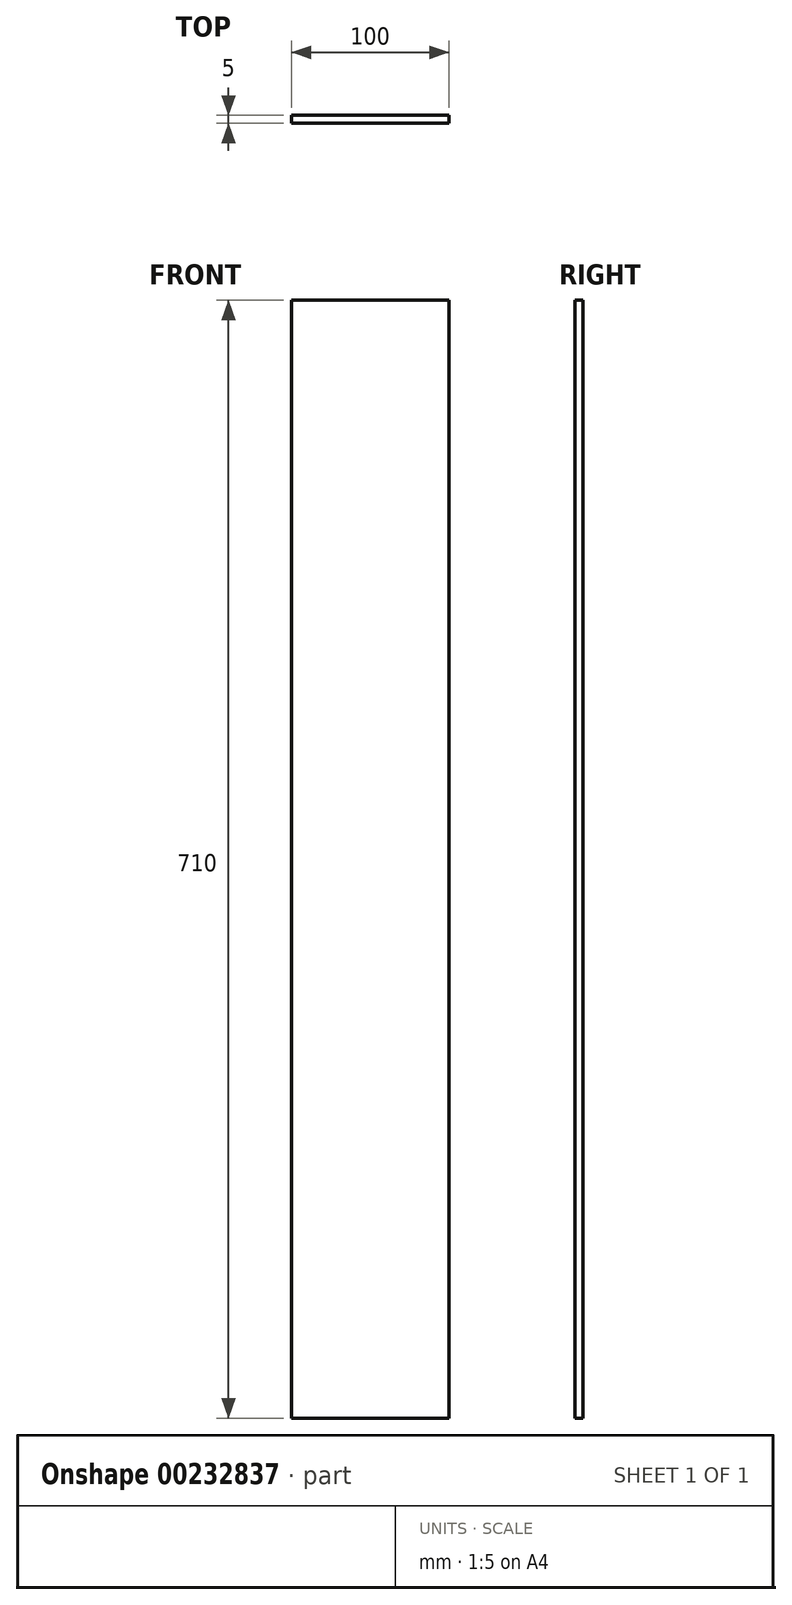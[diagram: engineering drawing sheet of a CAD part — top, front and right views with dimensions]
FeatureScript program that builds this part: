
annotation { "Feature Type Name" : "Feature", "Feature Type Description" : "" }
export const myFeature = defineFeature(function(context is Context, id is Id, definition is map)
    precondition{}
    {
        {
            var Q0;
            Q0=qCreatedBy(makeId("Front.planeOp"),FACE);
            var sketch = newSketch(context, id + "F0", { "sketchPlane" : qUnion([Q0])});
            skLineSegment(sketch, "E0.bottom", {"start": v(-6.67, 710.22) * mm, "end": v(93.33, 710.22) * mm});
            skLineSegment(sketch, "E0.top", {"start": v(-6.67, 0.22) * mm, "end": v(93.33, 0.22) * mm});
            skLineSegment(sketch, "E0.left", {"start": v(-6.67, 710.22) * mm, "end": v(-6.67, 0.22) * mm});
            skLineSegment(sketch, "E0.right", {"start": v(93.33, 710.22) * mm, "end": v(93.33, 0.22) * mm});
            skSolve(sketch);
        }
        {
            var Q0;
            Q0=makeQuery(id+"F0.imprint","IMPRINT",FACE,{"disambiguationData":[TD([[makeQuery(id+"F0.imprint","IMPRINT",EDGE,{"derivedFrom":sQuery(id+"F0.wireOp",EDGE,"E0.bottom")}),-1.0]])]});
            extrude(context, id + "F1", {"entities" : qUnion([Q0]), "depth" : 5 * mm});
        }
    });
